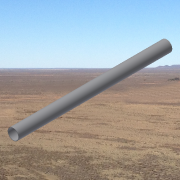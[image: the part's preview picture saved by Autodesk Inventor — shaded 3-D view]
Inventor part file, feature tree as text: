
AUTODESK INVENTOR PART (.ipt)
format: ipt  version: 2014 SP1 (Build 180222100, 222)  size: 123,904 bytes
history: native  units: in
note: dims shown in document units (in); Inventor stores cm internally (conversion verified against a paired STEP export)
features: extrude x1, sketch x1
ambient origin geometry x8: Origin, YZ Plane, XZ Plane, XY Plane, X Axis, Y Axis, Z Axis, Center Point
bodies: Solid1 (feature_tree)
feature tree (2):
  extrude  "Extrusion1"  Depth=59.0551in
  sketch  "Sketch1"  dims[d0=3.937in d1=0.175in d2=59.0551in d3=0.0in]
